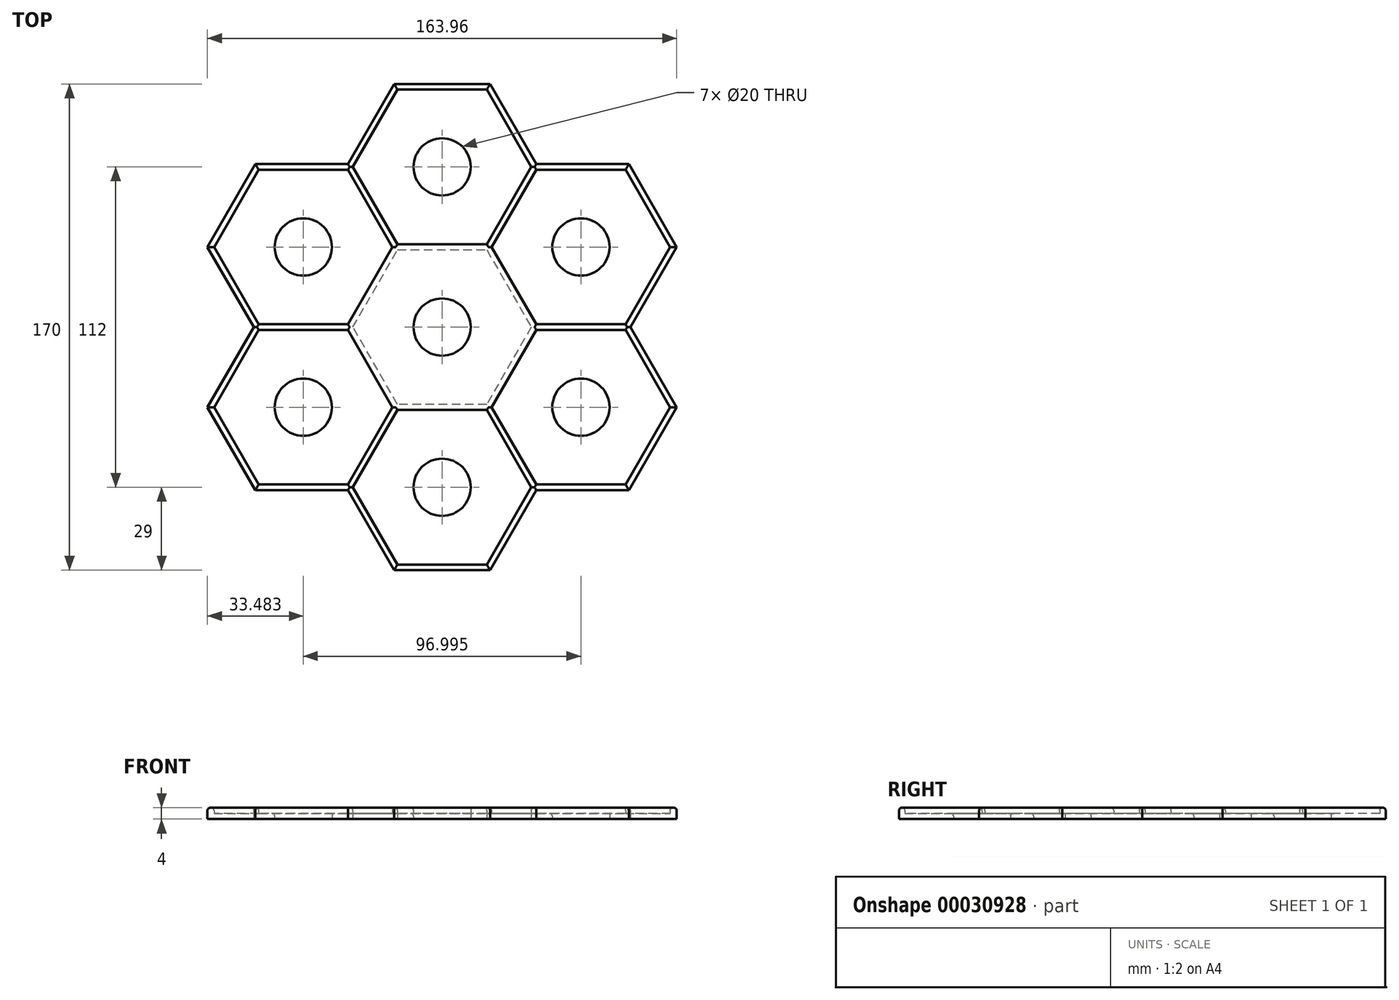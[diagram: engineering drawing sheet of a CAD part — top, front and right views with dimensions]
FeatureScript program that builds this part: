
annotation { "Feature Type Name" : "Feature", "Feature Type Description" : "" }
export const myFeature = defineFeature(function(context is Context, id is Id, definition is map)
    precondition{}
    {
        {
            var Q0;
            Q0=qCreatedBy(makeId("Top.planeOp"),FACE);
            var sketch = newSketch(context, id + "F0", { "sketchPlane" : qUnion([Q0])});
            skCircle(sketch, "E0.cCircle", {"center": v(0, 0) * mm, "radius": 27 * mm, "construction": true});
            skLineSegment(sketch, "E0.0", {"start": v(15.59, 27) * mm, "end": v(31.18, 0) * mm});
            skLineSegment(sketch, "E0.1", {"start": v(31.18, 0) * mm, "end": v(15.59, -27) * mm});
            skLineSegment(sketch, "E0.2", {"start": v(15.59, -27) * mm, "end": v(-15.59, -27) * mm});
            skLineSegment(sketch, "E0.3", {"start": v(-15.59, -27) * mm, "end": v(-31.18, 0) * mm});
            skLineSegment(sketch, "E0.4", {"start": v(-31.18, 0) * mm, "end": v(-15.59, 27) * mm});
            skLineSegment(sketch, "E0.5", {"start": v(-15.59, 27) * mm, "end": v(15.59, 27) * mm});
            skPoint(sketch, "E0.0.midPoint", {"position": v(23.38, 13.5) * mm});
            skCircle(sketch, "E1", {"center": v(0, 0) * mm, "radius": 10 * mm});
            skLineSegment(sketch, "E2.4", {"start": v(17.32, 28) * mm, "end": v(32.9, 55) * mm});
            skLineSegment(sketch, "E2.1", {"start": v(79.67, 28) * mm, "end": v(64.09, 1) * mm});
            skLineSegment(sketch, "E2.2", {"start": v(64.09, 1) * mm, "end": v(32.9, 1) * mm});
            skLineSegment(sketch, "E2.5", {"start": v(32.9, 55) * mm, "end": v(64.09, 55) * mm});
            skCircle(sketch, "E3", {"center": v(48.5, 28) * mm, "radius": 10 * mm});
            skLineSegment(sketch, "E2.3", {"start": v(32.9, 1) * mm, "end": v(17.32, 28) * mm});
            skLineSegment(sketch, "E2.0", {"start": v(64.09, 55) * mm, "end": v(79.67, 28) * mm});
            skCircle(sketch, "E2.cCircle", {"center": v(48.5, 28) * mm, "radius": 27 * mm, "construction": true});
            skPoint(sketch, "E2.0.midPoint", {"position": v(71.88, 41.5) * mm});
            skLineSegment(sketch, "E4.4", {"start": v(17.32, -28) * mm, "end": v(32.9, -1) * mm});
            skLineSegment(sketch, "E4.1", {"start": v(79.67, -28) * mm, "end": v(64.09, -55) * mm});
            skLineSegment(sketch, "E4.2", {"start": v(64.09, -55) * mm, "end": v(32.9, -55) * mm});
            skLineSegment(sketch, "E4.5", {"start": v(32.9, -1) * mm, "end": v(64.09, -1) * mm});
            skCircle(sketch, "E5", {"center": v(48.5, -28) * mm, "radius": 10 * mm});
            skLineSegment(sketch, "E4.3", {"start": v(32.9, -55) * mm, "end": v(17.32, -28) * mm});
            skLineSegment(sketch, "E4.0", {"start": v(64.09, -1) * mm, "end": v(79.67, -28) * mm});
            skCircle(sketch, "E4.cCircle", {"center": v(48.5, -28) * mm, "radius": 27 * mm, "construction": true});
            skPoint(sketch, "E4.0.midPoint", {"position": v(71.88, -14.5) * mm});
            skLineSegment(sketch, "E6.4", {"start": v(-31.18, -56) * mm, "end": v(-15.59, -29) * mm});
            skLineSegment(sketch, "E6.1", {"start": v(31.18, -56) * mm, "end": v(15.59, -83) * mm});
            skLineSegment(sketch, "E6.2", {"start": v(15.59, -83) * mm, "end": v(-15.59, -83) * mm});
            skLineSegment(sketch, "E6.5", {"start": v(-15.59, -29) * mm, "end": v(15.59, -29) * mm});
            skCircle(sketch, "E7", {"center": v(0, -56) * mm, "radius": 10 * mm});
            skLineSegment(sketch, "E6.3", {"start": v(-15.59, -83) * mm, "end": v(-31.18, -56) * mm});
            skLineSegment(sketch, "E6.0", {"start": v(15.59, -29) * mm, "end": v(31.18, -56) * mm});
            skCircle(sketch, "E6.cCircle", {"center": v(0, -56) * mm, "radius": 27 * mm, "construction": true});
            skPoint(sketch, "E6.0.midPoint", {"position": v(23.38, -42.5) * mm});
            skLineSegment(sketch, "E8.4", {"start": v(-79.67, -28) * mm, "end": v(-64.09, -1) * mm});
            skLineSegment(sketch, "E8.1", {"start": v(-17.32, -28) * mm, "end": v(-32.9, -55) * mm});
            skLineSegment(sketch, "E8.2", {"start": v(-32.9, -55) * mm, "end": v(-64.09, -55) * mm});
            skLineSegment(sketch, "E8.5", {"start": v(-64.09, -1) * mm, "end": v(-32.9, -1) * mm});
            skCircle(sketch, "E9", {"center": v(-48.5, -28) * mm, "radius": 10 * mm});
            skLineSegment(sketch, "E8.3", {"start": v(-64.09, -55) * mm, "end": v(-79.67, -28) * mm});
            skLineSegment(sketch, "E8.0", {"start": v(-32.9, -1) * mm, "end": v(-17.32, -28) * mm});
            skCircle(sketch, "E8.cCircle", {"center": v(-48.5, -28) * mm, "radius": 27 * mm, "construction": true});
            skPoint(sketch, "E8.0.midPoint", {"position": v(-25.11, -14.5) * mm});
            skLineSegment(sketch, "E10.4", {"start": v(-79.67, 28) * mm, "end": v(-64.09, 55) * mm});
            skLineSegment(sketch, "E10.1", {"start": v(-17.32, 28) * mm, "end": v(-32.9, 1) * mm});
            skLineSegment(sketch, "E10.2", {"start": v(-32.9, 1) * mm, "end": v(-64.09, 1) * mm});
            skLineSegment(sketch, "E10.5", {"start": v(-64.09, 55) * mm, "end": v(-32.9, 55) * mm});
            skCircle(sketch, "E11", {"center": v(-48.5, 28) * mm, "radius": 10 * mm});
            skLineSegment(sketch, "E10.3", {"start": v(-64.09, 1) * mm, "end": v(-79.67, 28) * mm});
            skLineSegment(sketch, "E10.0", {"start": v(-32.9, 55) * mm, "end": v(-17.32, 28) * mm});
            skCircle(sketch, "E10.cCircle", {"center": v(-48.5, 28) * mm, "radius": 27 * mm, "construction": true});
            skPoint(sketch, "E10.0.midPoint", {"position": v(-25.11, 41.5) * mm});
            skLineSegment(sketch, "E12.4", {"start": v(-31.18, 56) * mm, "end": v(-15.59, 83) * mm});
            skLineSegment(sketch, "E12.1", {"start": v(31.18, 56) * mm, "end": v(15.59, 29) * mm});
            skLineSegment(sketch, "E12.2", {"start": v(15.59, 29) * mm, "end": v(-15.59, 29) * mm});
            skLineSegment(sketch, "E12.5", {"start": v(-15.59, 83) * mm, "end": v(15.59, 83) * mm});
            skCircle(sketch, "E13", {"center": v(0, 56) * mm, "radius": 10 * mm});
            skLineSegment(sketch, "E12.3", {"start": v(-15.59, 29) * mm, "end": v(-31.18, 56) * mm});
            skLineSegment(sketch, "E12.0", {"start": v(15.59, 83) * mm, "end": v(31.18, 56) * mm});
            skCircle(sketch, "E12.cCircle", {"center": v(0, 56) * mm, "radius": 27 * mm, "construction": true});
            skPoint(sketch, "E12.0.midPoint", {"position": v(23.38, 69.5) * mm});
            skLineSegment(sketch, "E14", {"start": v(-15.59, 27) * mm, "end": v(-17.32, 28) * mm, "construction": true});
            skLineSegment(sketch, "E15", {"start": v(-65.82, 0) * mm, "end": v(-81.98, 28) * mm});
            skLineSegment(sketch, "E16", {"start": v(-81.98, 28) * mm, "end": v(-65.24, 57) * mm});
            skLineSegment(sketch, "E17", {"start": v(-65.24, 57) * mm, "end": v(-32.9, 57) * mm});
            skLineSegment(sketch, "E18", {"start": v(-32.9, 57) * mm, "end": v(-16.74, 85) * mm});
            skLineSegment(sketch, "E19", {"start": v(-16.74, 85) * mm, "end": v(16.74, 85) * mm});
            skLineSegment(sketch, "E20", {"start": v(16.74, 85) * mm, "end": v(32.9, 57) * mm});
            skLineSegment(sketch, "E21", {"start": v(32.9, 57) * mm, "end": v(65.24, 57) * mm});
            skLineSegment(sketch, "E22", {"start": v(65.24, 57) * mm, "end": v(81.98, 28) * mm});
            skLineSegment(sketch, "E23", {"start": v(81.98, 28) * mm, "end": v(65.82, 0) * mm});
            skLineSegment(sketch, "E24", {"start": v(65.82, 0) * mm, "end": v(81.98, -28) * mm});
            skLineSegment(sketch, "E25", {"start": v(81.98, -28) * mm, "end": v(65.24, -57) * mm});
            skLineSegment(sketch, "E26", {"start": v(65.24, -57) * mm, "end": v(32.9, -57) * mm});
            skLineSegment(sketch, "E27", {"start": v(32.9, -57) * mm, "end": v(16.74, -85) * mm});
            skLineSegment(sketch, "E28", {"start": v(16.74, -85) * mm, "end": v(-16.74, -85) * mm});
            skLineSegment(sketch, "E29", {"start": v(-16.74, -85) * mm, "end": v(-32.9, -57) * mm});
            skLineSegment(sketch, "E30", {"start": v(-32.9, -57) * mm, "end": v(-65.24, -57) * mm});
            skLineSegment(sketch, "E31", {"start": v(-65.24, -57) * mm, "end": v(-81.98, -28) * mm});
            skLineSegment(sketch, "E32", {"start": v(-81.98, -28) * mm, "end": v(-65.82, 0) * mm});
            skSolve(sketch);
        }
        {
            var Q0;
            Q0=makeQuery(id+"F0.imprint","IMPRINT",FACE,{"disambiguationData":[TD([[makeQuery(id+"F0.imprint","IMPRINT",EDGE,{"derivedFrom":sQuery(id+"F0.wireOp",EDGE,"E10.4")}),-1.0]])]});
            var Q1;
            Q1=makeQuery(id+"F0.imprint","IMPRINT",FACE,{"disambiguationData":[TD([[makeQuery(id+"F0.imprint","IMPRINT",EDGE,{"derivedFrom":sQuery(id+"F0.wireOp",EDGE,"E12.4")}),-1.0]])]});
            var Q2;
            Q2=makeQuery(id+"F0.imprint","IMPRINT",FACE,{"disambiguationData":[TD([[makeQuery(id+"F0.imprint","IMPRINT",EDGE,{"derivedFrom":sQuery(id+"F0.wireOp",EDGE,"E2.4")}),-1.0]])]});
            var Q3;
            Q3=makeQuery(id+"F0.imprint","IMPRINT",FACE,{"disambiguationData":[TD([[makeQuery(id+"F0.imprint","IMPRINT",EDGE,{"derivedFrom":sQuery(id+"F0.wireOp",EDGE,"E4.4")}),-1.0]])]});
            var Q4;
            Q4=makeQuery(id+"F0.imprint","IMPRINT",FACE,{"disambiguationData":[TD([[makeQuery(id+"F0.imprint","IMPRINT",EDGE,{"derivedFrom":sQuery(id+"F0.wireOp",EDGE,"E6.4")}),-1.0]])]});
            var Q5;
            Q5=makeQuery(id+"F0.imprint","IMPRINT",FACE,{"disambiguationData":[TD([[makeQuery(id+"F0.imprint","IMPRINT",EDGE,{"derivedFrom":sQuery(id+"F0.wireOp",EDGE,"E8.4")}),-1.0]])]});
            var Q6;
            Q6=sQuery(id+"F0.wireOp",EDGE,"E10.2");
            var Q7;
            Q7=sQuery(id+"F0.wireOp",EDGE,"E10.3");
            var Q8;
            Q8=sQuery(id+"F0.wireOp",EDGE,"E10.4");
            var Q9;
            Q9=sQuery(id+"F0.wireOp",EDGE,"E10.1");
            var Q10;
            Q10=sQuery(id+"F0.wireOp",EDGE,"E10.0");
            var Q11;
            Q11=sQuery(id+"F0.wireOp",EDGE,"E10.5");
            extrude(context, id + "F1", {"entities" : qUnion([Q0, Q1, Q2, Q3, Q4, Q5]), "surfaceEntities" : qUnion([Q6, Q7, Q8, Q9, Q10, Q11]), "depth" : 2 * mm});
        }
        {
            var Q0;
            Q0=makeQuery(id+"F0.imprint","IMPRINT",FACE,{"disambiguationData":[TD([[makeQuery(id+"F0.imprint","IMPRINT",EDGE,{"derivedFrom":sQuery(id+"F0.wireOp",EDGE,"E0.0")}),1.0]])]});
            extrude(context, id + "F2", {"entities" : qUnion([Q0]), "operationType" : NewBodyOperationType.ADD, "depth" : 4 * mm});
        }
        {
            var Q0;
            Q0=makeQuery(id+"F1.opExtrude","CAP_EDGE",EDGE,{"disambiguationData":[OSD([sQuery(id+"F0.wireOp",EDGE,"E7")])],"isStart":false});
            var Q1;
            Q1=makeQuery(id+"F1.opExtrude","CAP_EDGE",EDGE,{"disambiguationData":[OSD([sQuery(id+"F0.wireOp",EDGE,"E9")])],"isStart":false});
            var Q2;
            Q2=makeQuery(id+"F1.opExtrude","CAP_EDGE",EDGE,{"disambiguationData":[OSD([sQuery(id+"F0.wireOp",EDGE,"E1")])],"isStart":false});
            var Q3;
            Q3=makeQuery(id+"F1.opExtrude","CAP_EDGE",EDGE,{"disambiguationData":[OSD([sQuery(id+"F0.wireOp",EDGE,"E11")])],"isStart":false});
            var Q4;
            Q4=makeQuery(id+"F1.opExtrude","CAP_EDGE",EDGE,{"disambiguationData":[OSD([sQuery(id+"F0.wireOp",EDGE,"E13")])],"isStart":false});
            var Q5;
            Q5=makeQuery(id+"F1.opExtrude","CAP_EDGE",EDGE,{"disambiguationData":[OSD([sQuery(id+"F0.wireOp",EDGE,"E3")])],"isStart":false});
            var Q6;
            Q6=makeQuery(id+"F1.opExtrude","CAP_EDGE",EDGE,{"disambiguationData":[OSD([sQuery(id+"F0.wireOp",EDGE,"E5")])],"isStart":false});
            fillet(context, id + "F3", {"entities" : qUnion([Q0, Q1, Q2, Q3, Q4, Q5, Q6]), "radius" : 1 * mm, "tangentPropagation" : true, "allowEdgeOverflow" : false});
        }
        {
            var Q0;
            Q0=makeQuery(id+"F0.imprint","IMPRINT",FACE,{"disambiguationData":[TD([[makeQuery(id+"F0.imprint","IMPRINT",EDGE,{"derivedFrom":sQuery(id+"F0.wireOp",EDGE,"E0.0")}),-1.0]])]});
            extrude(context, id + "F4", {"entities" : qUnion([Q0]), "operationType" : NewBodyOperationType.ADD, "depth" : 4 * mm, "hasSecondDirection" : true, "secondDirectionOppositeDirection" : false, "secondDirectionDepth" : 2 * mm});
        }
        {
            var Q0;
            Q0=makeQuery(id+"F2.opExtrude","CAP_EDGE",EDGE,{"disambiguationData":[OSD([sQuery(id+"F0.wireOp",EDGE,"E16")])],"isStart":false});
            var Q1;
            Q1=makeQuery(id+"F2.opExtrude","CAP_EDGE",EDGE,{"disambiguationData":[OSD([sQuery(id+"F0.wireOp",EDGE,"E17")])],"isStart":false});
            var Q2;
            Q2=makeQuery(id+"F2.opExtrude","CAP_EDGE",EDGE,{"disambiguationData":[OSD([sQuery(id+"F0.wireOp",EDGE,"E18")])],"isStart":false});
            var Q3;
            Q3=makeQuery(id+"F2.opExtrude","CAP_EDGE",EDGE,{"disambiguationData":[OSD([sQuery(id+"F0.wireOp",EDGE,"E19")])],"isStart":false});
            var Q4;
            Q4=makeQuery(id+"F2.opExtrude","CAP_EDGE",EDGE,{"disambiguationData":[OSD([sQuery(id+"F0.wireOp",EDGE,"E20")])],"isStart":false});
            var Q5;
            Q5=makeQuery(id+"F2.opExtrude","CAP_EDGE",EDGE,{"disambiguationData":[OSD([sQuery(id+"F0.wireOp",EDGE,"E21")])],"isStart":false});
            var Q6;
            Q6=makeQuery(id+"F2.opExtrude","CAP_EDGE",EDGE,{"disambiguationData":[OSD([sQuery(id+"F0.wireOp",EDGE,"E22")])],"isStart":false});
            var Q7;
            Q7=makeQuery(id+"F2.opExtrude","CAP_EDGE",EDGE,{"disambiguationData":[OSD([sQuery(id+"F0.wireOp",EDGE,"E15")])],"isStart":false});
            var Q8;
            Q8=makeQuery(id+"F2.opExtrude","CAP_EDGE",EDGE,{"disambiguationData":[OSD([sQuery(id+"F0.wireOp",EDGE,"E32")])],"isStart":false});
            var Q9;
            Q9=makeQuery(id+"F2.opExtrude","CAP_EDGE",EDGE,{"disambiguationData":[OSD([sQuery(id+"F0.wireOp",EDGE,"E31")])],"isStart":false});
            var Q10;
            Q10=makeQuery(id+"F2.opExtrude","CAP_EDGE",EDGE,{"disambiguationData":[OSD([sQuery(id+"F0.wireOp",EDGE,"E30")])],"isStart":false});
            var Q11;
            Q11=makeQuery(id+"F2.opExtrude","CAP_EDGE",EDGE,{"disambiguationData":[OSD([sQuery(id+"F0.wireOp",EDGE,"E29")])],"isStart":false});
            var Q12;
            Q12=makeQuery(id+"F2.opExtrude","CAP_EDGE",EDGE,{"disambiguationData":[OSD([sQuery(id+"F0.wireOp",EDGE,"E28")])],"isStart":false});
            var Q13;
            Q13=makeQuery(id+"F2.opExtrude","CAP_EDGE",EDGE,{"disambiguationData":[OSD([sQuery(id+"F0.wireOp",EDGE,"E27")])],"isStart":false});
            var Q14;
            Q14=makeQuery(id+"F2.opExtrude","CAP_EDGE",EDGE,{"disambiguationData":[OSD([sQuery(id+"F0.wireOp",EDGE,"E26")])],"isStart":false});
            var Q15;
            Q15=makeQuery(id+"F2.opExtrude","CAP_EDGE",EDGE,{"disambiguationData":[OSD([sQuery(id+"F0.wireOp",EDGE,"E25")])],"isStart":false});
            var Q16;
            Q16=makeQuery(id+"F2.opExtrude","CAP_EDGE",EDGE,{"disambiguationData":[OSD([sQuery(id+"F0.wireOp",EDGE,"E24")])],"isStart":false});
            var Q17;
            Q17=makeQuery(id+"F2.opExtrude","CAP_EDGE",EDGE,{"disambiguationData":[OSD([sQuery(id+"F0.wireOp",EDGE,"E23")])],"isStart":false});
            fillet(context, id + "F5", {"entities" : qUnion([Q0, Q1, Q2, Q3, Q4, Q5, Q6, Q7, Q8, Q9, Q10, Q11, Q12, Q13, Q14, Q15, Q16, Q17]), "radius" : 1 * mm, "tangentPropagation" : true, "allowEdgeOverflow" : false});
        }
        {
            var Q0;
            Q0=makeQuery(id+"F2.opExtrude","CAP_EDGE",EDGE,{"disambiguationData":[OSD([sQuery(id+"F0.wireOp",EDGE,"E15")])],"isStart":false});
            var Q1;
            Q1=makeQuery(id+"F2.opExtrude","CAP_EDGE",EDGE,{"disambiguationData":[OSD([sQuery(id+"F0.wireOp",EDGE,"E16")])],"isStart":false});
            var Q2;
            Q2=makeQuery(id+"F2.opExtrude","CAP_EDGE",EDGE,{"disambiguationData":[OSD([sQuery(id+"F0.wireOp",EDGE,"E17")])],"isStart":false});
            var Q3;
            Q3=makeQuery(id+"F2.opExtrude","CAP_EDGE",EDGE,{"disambiguationData":[OSD([sQuery(id+"F0.wireOp",EDGE,"E32")])],"isStart":false});
            var Q4;
            Q4=makeQuery(id+"F2.opExtrude","CAP_EDGE",EDGE,{"disambiguationData":[OSD([sQuery(id+"F0.wireOp",EDGE,"E31")])],"isStart":false});
            var Q5;
            Q5=makeQuery(id+"F2.opExtrude","CAP_EDGE",EDGE,{"disambiguationData":[OSD([sQuery(id+"F0.wireOp",EDGE,"E30")])],"isStart":false});
            var Q6;
            Q6=makeQuery(id+"F2.opExtrude","CAP_EDGE",EDGE,{"disambiguationData":[OSD([sQuery(id+"F0.wireOp",EDGE,"E29")])],"isStart":false});
            var Q7;
            Q7=makeQuery(id+"F2.opExtrude","CAP_EDGE",EDGE,{"disambiguationData":[OSD([sQuery(id+"F0.wireOp",EDGE,"E28")])],"isStart":false});
            var Q8;
            Q8=makeQuery(id+"F2.opExtrude","CAP_EDGE",EDGE,{"disambiguationData":[OSD([sQuery(id+"F0.wireOp",EDGE,"E27")])],"isStart":false});
            var Q9;
            Q9=makeQuery(id+"F2.opExtrude","CAP_EDGE",EDGE,{"disambiguationData":[OSD([sQuery(id+"F0.wireOp",EDGE,"E26")])],"isStart":false});
            var Q10;
            Q10=makeQuery(id+"F2.opExtrude","CAP_EDGE",EDGE,{"disambiguationData":[OSD([sQuery(id+"F0.wireOp",EDGE,"E25")])],"isStart":false});
            var Q11;
            Q11=makeQuery(id+"F2.opExtrude","CAP_EDGE",EDGE,{"disambiguationData":[OSD([sQuery(id+"F0.wireOp",EDGE,"E24")])],"isStart":false});
            var Q12;
            Q12=makeQuery(id+"F2.opExtrude","CAP_EDGE",EDGE,{"disambiguationData":[OSD([sQuery(id+"F0.wireOp",EDGE,"E23")])],"isStart":false});
            var Q13;
            Q13=makeQuery(id+"F2.opExtrude","CAP_EDGE",EDGE,{"disambiguationData":[OSD([sQuery(id+"F0.wireOp",EDGE,"E22")])],"isStart":false});
            var Q14;
            Q14=makeQuery(id+"F2.opExtrude","CAP_EDGE",EDGE,{"disambiguationData":[OSD([sQuery(id+"F0.wireOp",EDGE,"E21")])],"isStart":false});
            var Q15;
            Q15=makeQuery(id+"F2.opExtrude","CAP_EDGE",EDGE,{"disambiguationData":[OSD([sQuery(id+"F0.wireOp",EDGE,"E20")])],"isStart":false});
            var Q16;
            Q16=makeQuery(id+"F2.opExtrude","CAP_EDGE",EDGE,{"disambiguationData":[OSD([sQuery(id+"F0.wireOp",EDGE,"E19")])],"isStart":false});
            var Q17;
            Q17=makeQuery(id+"F2.opExtrude","CAP_EDGE",EDGE,{"disambiguationData":[OSD([sQuery(id+"F0.wireOp",EDGE,"E18")])],"isStart":false});
            var Q18;
            Q18=makeQuery(id+"F2.opExtrude","CAP_EDGE",EDGE,{"disambiguationData":[OSD([sQuery(id+"F0.wireOp",EDGE,"E8.5")])],"isStart":false});
            var Q19;
            Q19=makeQuery(id+"F2.opExtrude","CAP_EDGE",EDGE,{"disambiguationData":[OSD([sQuery(id+"F0.wireOp",EDGE,"E10.2")])],"isStart":false});
            var Q20;
            Q20=makeQuery(id+"F2.opExtrude","CAP_EDGE",EDGE,{"disambiguationData":[OSD([sQuery(id+"F0.wireOp",EDGE,"E8.0")])],"isStart":false});
            var Q21;
            Q21=makeQuery(id+"F2.opExtrude","CAP_EDGE",EDGE,{"disambiguationData":[OSD([sQuery(id+"F0.wireOp",EDGE,"E0.3")])],"isStart":false});
            var Q22;
            Q22=makeQuery(id+"F2.opExtrude","CAP_EDGE",EDGE,{"disambiguationData":[OSD([sQuery(id+"F0.wireOp",EDGE,"E0.4")])],"isStart":false});
            var Q23;
            Q23=makeQuery(id+"F2.opExtrude","CAP_EDGE",EDGE,{"disambiguationData":[OSD([sQuery(id+"F0.wireOp",EDGE,"E10.1")])],"isStart":false});
            var Q24;
            Q24=makeQuery(id+"F2.opExtrude","CAP_EDGE",EDGE,{"disambiguationData":[OSD([sQuery(id+"F0.wireOp",EDGE,"E8.1")])],"isStart":false});
            var Q25;
            Q25=makeQuery(id+"F2.opExtrude","CAP_EDGE",EDGE,{"disambiguationData":[OSD([sQuery(id+"F0.wireOp",EDGE,"E6.4")])],"isStart":false});
            var Q26;
            Q26=makeQuery(id+"F2.opExtrude","CAP_EDGE",EDGE,{"disambiguationData":[OSD([sQuery(id+"F0.wireOp",EDGE,"E6.5")])],"isStart":false});
            var Q27;
            Q27=makeQuery(id+"F2.opExtrude","CAP_EDGE",EDGE,{"disambiguationData":[OSD([sQuery(id+"F0.wireOp",EDGE,"E0.2")])],"isStart":false});
            var Q28;
            Q28=makeQuery(id+"F2.opExtrude","CAP_EDGE",EDGE,{"disambiguationData":[OSD([sQuery(id+"F0.wireOp",EDGE,"E6.0")])],"isStart":false});
            var Q29;
            Q29=makeQuery(id+"F2.opExtrude","CAP_EDGE",EDGE,{"disambiguationData":[OSD([sQuery(id+"F0.wireOp",EDGE,"E4.3")])],"isStart":false});
            var Q30;
            Q30=makeQuery(id+"F2.opExtrude","CAP_EDGE",EDGE,{"disambiguationData":[OSD([sQuery(id+"F0.wireOp",EDGE,"E4.4")])],"isStart":false});
            var Q31;
            Q31=makeQuery(id+"F2.opExtrude","CAP_EDGE",EDGE,{"disambiguationData":[OSD([sQuery(id+"F0.wireOp",EDGE,"E0.1")])],"isStart":false});
            var Q32;
            Q32=makeQuery(id+"F2.opExtrude","CAP_EDGE",EDGE,{"disambiguationData":[OSD([sQuery(id+"F0.wireOp",EDGE,"E6.1")])],"isStart":false});
            var Q33;
            Q33=makeQuery(id+"F2.opExtrude","CAP_EDGE",EDGE,{"disambiguationData":[OSD([sQuery(id+"F0.wireOp",EDGE,"E6.2")])],"isStart":false});
            var Q34;
            Q34=makeQuery(id+"F2.opExtrude","CAP_EDGE",EDGE,{"disambiguationData":[OSD([sQuery(id+"F0.wireOp",EDGE,"E6.3")])],"isStart":false});
            var Q35;
            Q35=makeQuery(id+"F2.opExtrude","CAP_EDGE",EDGE,{"disambiguationData":[OSD([sQuery(id+"F0.wireOp",EDGE,"E10.0")])],"isStart":false});
            var Q36;
            Q36=makeQuery(id+"F2.opExtrude","CAP_EDGE",EDGE,{"disambiguationData":[OSD([sQuery(id+"F0.wireOp",EDGE,"E12.3")])],"isStart":false});
            var Q37;
            Q37=makeQuery(id+"F2.opExtrude","CAP_EDGE",EDGE,{"disambiguationData":[OSD([sQuery(id+"F0.wireOp",EDGE,"E0.5")])],"isStart":false});
            var Q38;
            Q38=makeQuery(id+"F2.opExtrude","CAP_EDGE",EDGE,{"disambiguationData":[OSD([sQuery(id+"F0.wireOp",EDGE,"E12.2")])],"isStart":false});
            var Q39;
            Q39=makeQuery(id+"F2.opExtrude","CAP_EDGE",EDGE,{"disambiguationData":[OSD([sQuery(id+"F0.wireOp",EDGE,"E0.0")])],"isStart":false});
            var Q40;
            Q40=makeQuery(id+"F2.opExtrude","CAP_EDGE",EDGE,{"disambiguationData":[OSD([sQuery(id+"F0.wireOp",EDGE,"E2.3")])],"isStart":false});
            var Q41;
            Q41=makeQuery(id+"F2.opExtrude","CAP_EDGE",EDGE,{"disambiguationData":[OSD([sQuery(id+"F0.wireOp",EDGE,"E12.4")])],"isStart":false});
            var Q42;
            Q42=makeQuery(id+"F2.opExtrude","CAP_EDGE",EDGE,{"disambiguationData":[OSD([sQuery(id+"F0.wireOp",EDGE,"E12.5")])],"isStart":false});
            var Q43;
            Q43=makeQuery(id+"F2.opExtrude","CAP_EDGE",EDGE,{"disambiguationData":[OSD([sQuery(id+"F0.wireOp",EDGE,"E12.0")])],"isStart":false});
            var Q44;
            Q44=makeQuery(id+"F2.opExtrude","CAP_EDGE",EDGE,{"disambiguationData":[OSD([sQuery(id+"F0.wireOp",EDGE,"E12.1")])],"isStart":false});
            var Q45;
            Q45=makeQuery(id+"F2.opExtrude","CAP_EDGE",EDGE,{"disambiguationData":[OSD([sQuery(id+"F0.wireOp",EDGE,"E2.4")])],"isStart":false});
            var Q46;
            Q46=makeQuery(id+"F2.opExtrude","CAP_EDGE",EDGE,{"disambiguationData":[OSD([sQuery(id+"F0.wireOp",EDGE,"E2.5")])],"isStart":false});
            var Q47;
            Q47=makeQuery(id+"F2.opExtrude","CAP_EDGE",EDGE,{"disambiguationData":[OSD([sQuery(id+"F0.wireOp",EDGE,"E2.1")])],"isStart":false});
            var Q48;
            Q48=makeQuery(id+"F2.opExtrude","CAP_EDGE",EDGE,{"disambiguationData":[OSD([sQuery(id+"F0.wireOp",EDGE,"E4.5")])],"isStart":false});
            var Q49;
            Q49=makeQuery(id+"F2.opExtrude","CAP_EDGE",EDGE,{"disambiguationData":[OSD([sQuery(id+"F0.wireOp",EDGE,"E4.0")])],"isStart":false});
            var Q50;
            Q50=makeQuery(id+"F2.opExtrude","CAP_EDGE",EDGE,{"disambiguationData":[OSD([sQuery(id+"F0.wireOp",EDGE,"E2.2")])],"isStart":false});
            var Q51;
            Q51=makeQuery(id+"F2.opExtrude","CAP_EDGE",EDGE,{"disambiguationData":[OSD([sQuery(id+"F0.wireOp",EDGE,"E2.0")])],"isStart":false});
            var Q52;
            Q52=makeQuery(id+"F2.opExtrude","CAP_EDGE",EDGE,{"disambiguationData":[OSD([sQuery(id+"F0.wireOp",EDGE,"E4.2")])],"isStart":false});
            var Q53;
            Q53=makeQuery(id+"F2.opExtrude","CAP_EDGE",EDGE,{"disambiguationData":[OSD([sQuery(id+"F0.wireOp",EDGE,"E4.1")])],"isStart":false});
            var Q54;
            Q54=makeQuery(id+"F2.opExtrude","CAP_EDGE",EDGE,{"disambiguationData":[OSD([sQuery(id+"F0.wireOp",EDGE,"E10.5")])],"isStart":false});
            var Q55;
            Q55=makeQuery(id+"F2.opExtrude","CAP_EDGE",EDGE,{"disambiguationData":[OSD([sQuery(id+"F0.wireOp",EDGE,"E10.4")])],"isStart":false});
            var Q56;
            Q56=makeQuery(id+"F2.opExtrude","CAP_EDGE",EDGE,{"disambiguationData":[OSD([sQuery(id+"F0.wireOp",EDGE,"E10.3")])],"isStart":false});
            var Q57;
            Q57=makeQuery(id+"F2.opExtrude","CAP_EDGE",EDGE,{"disambiguationData":[OSD([sQuery(id+"F0.wireOp",EDGE,"E8.2")])],"isStart":false});
            var Q58;
            Q58=makeQuery(id+"F2.opExtrude","CAP_EDGE",EDGE,{"disambiguationData":[OSD([sQuery(id+"F0.wireOp",EDGE,"E8.3")])],"isStart":false});
            var Q59;
            Q59=makeQuery(id+"F2.opExtrude","CAP_EDGE",EDGE,{"disambiguationData":[OSD([sQuery(id+"F0.wireOp",EDGE,"E8.4")])],"isStart":false});
            var Q60;
            Q60=makeQuery(id+"F4.opExtrude","CAP_EDGE",EDGE,{"disambiguationData":[OSD([sQuery(id+"F0.wireOp",EDGE,"E1")])],"isStart":false});
            fillet(context, id + "F6", {"entities" : qUnion([Q0, Q1, Q2, Q3, Q4, Q5, Q6, Q7, Q8, Q9, Q10, Q11, Q12, Q13, Q14, Q15, Q16, Q17, Q18, Q19, Q20, Q21, Q22, Q23, Q24, Q25, Q26, Q27, Q28, Q29, Q30, Q31, Q32, Q33, Q34, Q35, Q36, Q37, Q38, Q39, Q40, Q41, Q42, Q43, Q44, Q45, Q46, Q47, Q48, Q49, Q50, Q51, Q52, Q53, Q54, Q55, Q56, Q57, Q58, Q59, Q60]), "radius" : 1 * mm, "tangentPropagation" : true, "allowEdgeOverflow" : false});
        }
    });
